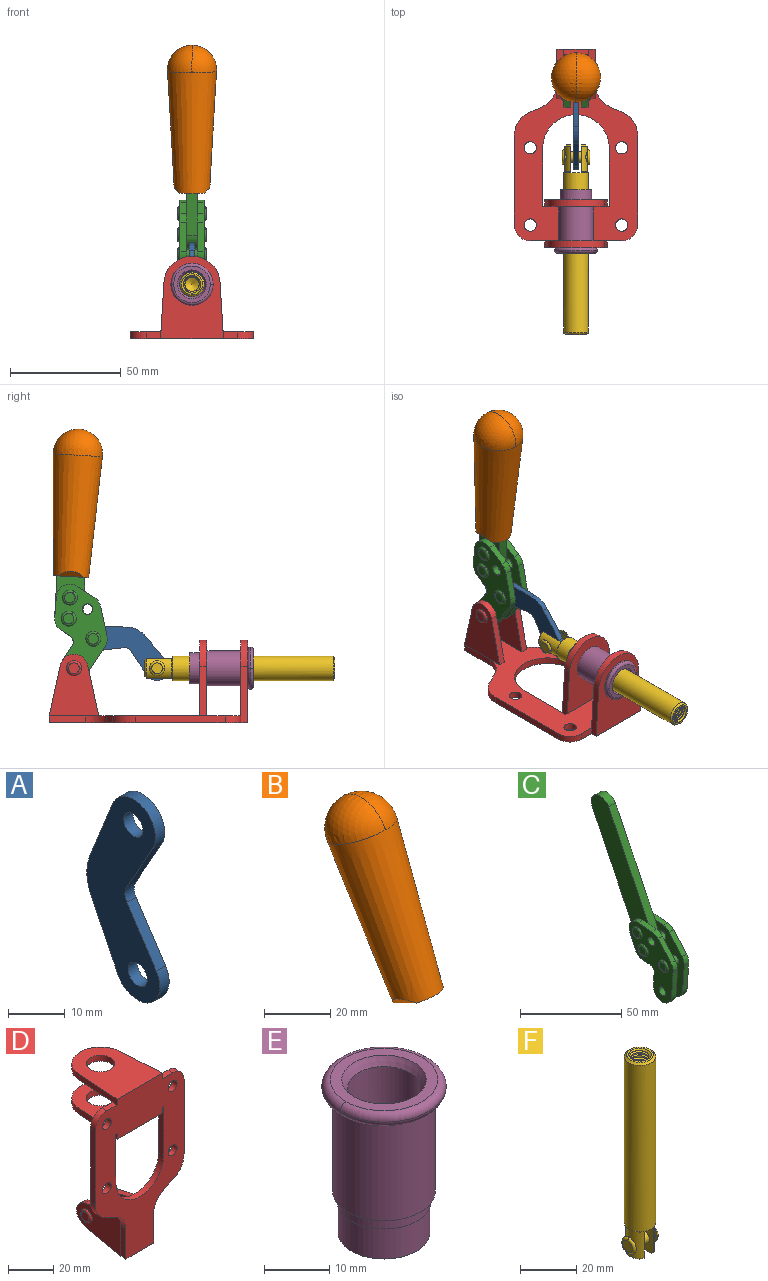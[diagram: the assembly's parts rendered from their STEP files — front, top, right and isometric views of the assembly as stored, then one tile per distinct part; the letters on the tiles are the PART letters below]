
ASSEMBLY  parts=6 mates=6
PART A: 12 faces, bbox 2.3x18.2x42.8 mm
  f0: cylinder r=2.4mm len=4.8mm, axis (1,0,0), area 34.9mm2, adj f4,f11
  f1: cylinder r=10.41mm len=8.47mm, axis (1,0,0), area 20.2mm2, adj f4,f9,f10,f11
  f2: cylinder r=3.05mm len=3.16mm, axis (1,0,0), area 7.7mm2, adj f4,f6,f7,f11
  f3: cylinder r=2.4mm len=4.8mm, axis (1,0,0), area 34.9mm2, adj f4,f11
  f4: plane 42.81x18.23mm, normal (-1,0,0), area 414.1mm2, adj f0,f1,f2,f3,f5,f6,f7,f8
  f5: cylinder r=5.54mm len=10.67mm, axis (1,0,0), area 41.8mm2, adj f4,f6,f10,f11
  f6: plane 11.66x6.53mm, normal (0,-0.87,-0.49), area 30.9mm2, adj f2,f4,f5,f11
  f7: plane 11.17x7.33mm, normal (0,-0.84,0.55), area 30.9mm2, adj f2,f4,f8,f11
  f8: cylinder r=5.54mm len=10.51mm, axis (1,0,0), area 41.8mm2, adj f4,f7,f9,f11
  f9: plane 13.67x6.67mm, normal (0,0.9,-0.44), area 35.1mm2, adj f1,f4,f8,f11
  f10: plane 14.1x5.7mm, normal (0,0.93,0.37), area 35.1mm2, adj f1,f4,f5,f11
  f11: plane 42.81x18.23mm, normal (1,0,0), area 414.1mm2, adj f0,f1,f2,f3,f5,f6,f7,f8
PART B: 11 faces, bbox 22.3x42.6x64.5 mm
  f0: sphere r=11.13mm, area 411.4mm2, adj f1,f8
  f1: cone r=11.11mm half-angle=3.3deg, axis (0,0.44,0.9), area 3251.8mm2, adj f0,f7,f8,f9,f10
  f2: cylinder r=6.16mm len=11.7mm, axis (1,0,0), area 89.5mm2, adj f3,f4,f5,f6
  f3: plane 60.23x36.75mm, normal (-1,0,0), area 763.6mm2, adj f2,f4,f6,f10
  f4: plane 51.37x25.05mm, normal (0,0.9,-0.44), area 264.2mm2, adj f2,f3,f5,f10
  f5: plane 60.23x36.75mm, normal (1,0,0), area 763.6mm2, adj f2,f4,f6,f10
  f6: plane 51.37x25.05mm, normal (0,-0.9,0.44), area 264.2mm2, adj f2,f3,f5,f10
  f7: plane 9.95x5.95mm, normal (0.71,-0.31,-0.64), area 25.8mm2, adj f1,f10
  f8: sphere r=11.13mm, area 411.4mm2, adj f0,f1
  f9: plane 9.95x5.95mm, normal (-0.71,-0.31,-0.64), area 25.8mm2, adj f1,f10
  f10: plane 14.27x11.38mm, normal (0,-0.44,-0.9), area 106.7mm2, adj f1,f3,f4,f5,f6,f7,f9
PART C: 59 faces, bbox 12.9x60.2x99.6 mm
  f0: torus R=2.39mm, axis (-1,0,0), area 14.9mm2, adj f20,f43,f51
  f1: torus R=2.39mm, axis (-1,0,0), area 14.9mm2, adj f19,f42,f51
  f2: torus R=2.39mm, axis (-1,0,0), area 14.9mm2, adj f18,f35,f51
  f3: torus R=2.39mm, axis (-1,0,0), area 14.9mm2, adj f14,f17,f23
  f4: torus R=2.39mm, axis (-1,0,0), area 14.9mm2, adj f13,f16,f23
  f5: torus R=2.39mm, axis (-1,0,0), area 14.9mm2, adj f12,f15,f23
  f6: cylinder r=2.39mm len=4.78mm, axis (1,0,0), area 46.5mm2, adj f48,f50,f51
  f7: cylinder r=2.39mm len=4.78mm, axis (1,0,0), area 46.5mm2, adj f50,f51
  f8: cylinder r=6.35mm len=12.68mm, axis (1,0,0), area 61.8mm2, adj f38,f39,f50,f51
  f9: cylinder r=2.39mm len=4.78mm, axis (-1,0,0), area 70.5mm2, adj f46,f50
  f10: cylinder r=2.39mm len=4.78mm, axis (-1,0,0), area 46.5mm2, adj f23,f45,f46
  f11: cylinder r=2.39mm len=4.78mm, axis (-1,0,0), area 46.5mm2, adj f23,f46
  f12: plane 4.78x4.78mm, normal (1,0,0), area 17.9mm2, adj f5,f15
  f13: plane 4.78x4.78mm, normal (1,0,0), area 17.9mm2, adj f4,f16
  f14: plane 4.78x4.78mm, normal (1,0,0), area 17.9mm2, adj f3,f17
  f15: torus R=2.39mm, axis (-1,0,0), area 14.9mm2, adj f5,f12,f23
  f16: torus R=2.39mm, axis (-1,0,0), area 14.9mm2, adj f4,f13,f23
  f17: torus R=2.39mm, axis (-1,0,0), area 14.9mm2, adj f3,f14,f23
  f18: plane 4.78x4.78mm, normal (-1,0,0), area 17.9mm2, adj f2,f35
  f19: plane 4.78x4.78mm, normal (-1,0,0), area 17.9mm2, adj f1,f42
  f20: plane 4.78x4.78mm, normal (-1,0,0), area 17.9mm2, adj f0,f43
  f21: plane 2.26x0.2mm, normal (1,0,0), area 0.2mm2, adj f31,f44
  f22: plane 2.26x0.2mm, normal (-1,0,0), area 0.2mm2, adj f41,f44
  f23: plane 39.37x30.77mm, normal (1,0,0), area 565.5mm2, adj f3,f4,f5,f10,f11,f15,f16,f17
  f24: cylinder r=6.1mm len=4.15mm, axis (-1,0,0), area 14.7mm2, adj f23,f25,f32,f46
  f25: plane 10.25x9.01mm, normal (0,-0.75,0.66), area 42.3mm2, adj f23,f24,f26,f46
  f26: cylinder r=6.35mm len=4.64mm, axis (-1,0,0), area 15.6mm2, adj f23,f25,f27,f46
  f27: plane 15.84x3.1mm, normal (0,-1,-0.07), area 49.2mm2, adj f23,f26,f28,f46
  f28: cylinder r=6.35mm len=12.68mm, axis (-1,0,0), area 61.8mm2, adj f23,f27,f29,f46
  f29: plane 8.11x3.1mm, normal (0,1,0.07), area 25.2mm2, adj f23,f28,f30,f46
  f30: cylinder r=3.05mm len=3.25mm, axis (-1,0,0), area 14.8mm2, adj f23,f29,f31,f46
  f31: plane 5.99x3.1mm, normal (0,0.07,-1), area 18.6mm2, adj f21,f23,f30,f44,f46
  f32: plane 9.5x3.1mm, normal (0,-0.07,1), area 29.5mm2, adj f23,f24,f33,f46,f47
  f33: cylinder r=6.1mm len=8.63mm, axis (-1,0,0), area 39.1mm2, adj f23,f32,f34,f47
  f34: plane 8.65x3.96mm, normal (0,0.91,-0.42), area 29.5mm2, adj f23,f33,f44,f47
  f35: torus R=2.39mm, axis (-1,0,0), area 14.9mm2, adj f2,f18,f51
  f36: plane 10.25x9.01mm, normal (0,-0.75,0.66), area 42.3mm2, adj f37,f49,f50,f51
  f37: cylinder r=6.35mm len=4.64mm, axis (1,0,0), area 15.6mm2, adj f36,f38,f50,f51
  f38: plane 15.84x3.1mm, normal (0,-1,-0.07), area 49.2mm2, adj f8,f37,f50,f51
  f39: plane 8.11x3.1mm, normal (0,1,0.07), area 25.2mm2, adj f8,f40,f50,f51
  f40: cylinder r=3.05mm len=3.25mm, axis (1,0,0), area 14.8mm2, adj f39,f41,f50,f51
  f41: plane 5.99x3.1mm, normal (0,0.07,-1), area 18.6mm2, adj f22,f40,f44,f50,f51
  f42: torus R=2.39mm, axis (-1,0,0), area 14.9mm2, adj f1,f19,f51
  f43: torus R=2.39mm, axis (-1,0,0), area 14.9mm2, adj f0,f20,f51
  f44: cylinder r=6.35mm len=12.12mm, axis (-1,0,0), area 128.9mm2, adj f21,f22,f23,f31,f34,f41,f46,f47
  f45: plane 2.65x1.35mm, normal (1,0,0), area 1mm2, adj f10,f55
  f46: plane 39.08x20.42mm, normal (-1,0,0), area 412.5mm2, adj f9,f10,f11,f24,f25,f26,f27,f28
  f47: plane 77.62x39.82mm, normal (1,0,0), area 850mm2, adj f32,f33,f34,f44,f53,f54,f55
  f48: plane 2.65x1.35mm, normal (-1,0,0), area 1mm2, adj f6,f55
  f49: cylinder r=6.1mm len=4.15mm, axis (1,0,0), area 14.7mm2, adj f36,f50,f51,f56
  f50: plane 39.08x20.42mm, normal (1,0,0), area 412.5mm2, adj f6,f7,f8,f9,f36,f37,f38,f39
  f51: plane 39.37x30.77mm, normal (-1,0,0), area 565.5mm2, adj f0,f1,f2,f6,f7,f8,f35,f36
  f52: plane 8.65x3.96mm, normal (0,0.91,-0.42), area 29.5mm2, adj f44,f51,f57,f58
  f53: plane 68.49x33.4mm, normal (0,0.9,-0.44), area 358.1mm2, adj f44,f47,f54,f58
  f54: cylinder r=6.35mm len=12.06mm, axis (1,0,0), area 93.7mm2, adj f47,f53,f55,f58
  f55: plane 68.49x33.4mm, normal (0,-0.9,0.44), area 358.1mm2, adj f44,f45,f46,f47,f48,f50,f54,f58
  f56: plane 9.5x3.1mm, normal (0,-0.07,1), area 29.5mm2, adj f49,f50,f51,f57,f58
  f57: cylinder r=6.1mm len=8.63mm, axis (1,0,0), area 39.1mm2, adj f51,f52,f56,f58
  f58: plane 77.62x39.82mm, normal (-1,0,0), area 850mm2, adj f44,f52,f53,f54,f55,f56,f57
PART D: 55 faces, bbox 55.7x37.4x89.8 mm
  f0: torus R=2.41mm, axis (-1,0,0), area 15mm2, adj f11,f15,f25
  f1: torus R=2.41mm, axis (-1,0,0), area 15mm2, adj f10,f12,f22
  f2: cylinder r=2.78mm len=5.56mm, axis (0,-1,0), area 54.2mm2, adj f30,f54
  f3: cylinder r=14.99mm len=29.97mm, axis (0,-1,0), area 145.9mm2, adj f30,f49,f53,f54
  f4: cylinder r=2.78mm len=5.56mm, axis (0,-1,0), area 54.2mm2, adj f30,f54
  f5: cylinder r=2.78mm len=5.56mm, axis (0,-1,0), area 54.2mm2, adj f30,f54
  f6: cylinder r=2.78mm len=5.56mm, axis (0,-1,0), area 54.2mm2, adj f30,f54
  f7: cylinder r=6.35mm len=12.7mm, axis (0,0,1), area 123.6mm2, adj f27,f51
  f8: cylinder r=6.35mm len=12.7mm, axis (0,0,-1), area 124.7mm2, adj f21,f35
  f9: cylinder r=2.41mm len=11.18mm, axis (-1,0,0), area 169.4mm2, adj f16,f19
  f10: plane 4.83x4.83mm, normal (1,0,0), area 18.3mm2, adj f1,f12
  f11: plane 4.83x4.83mm, normal (-1,0,0), area 18.3mm2, adj f0,f15
  f12: torus R=2.41mm, axis (-1,0,0), area 15mm2, adj f1,f10,f22
  f13: cylinder r=6.35mm len=12.41mm, axis (1,0,0), area 53.4mm2, adj f18,f19,f22,f23
  f14: cylinder r=6.35mm len=12.41mm, axis (-1,0,0), area 53.4mm2, adj f16,f17,f24,f25
  f15: torus R=2.41mm, axis (-1,0,0), area 15mm2, adj f0,f11,f25
  f16: plane 27.86x22.35mm, normal (1,0,0), area 425.4mm2, adj f9,f14,f17,f24,f30
  f17: plane 22.86x4.97mm, normal (0,0.21,0.98), area 72.5mm2, adj f14,f16,f25,f30
  f18: plane 22.86x4.97mm, normal (0,0.21,0.98), area 72.5mm2, adj f13,f19,f22,f30
  f19: plane 27.86x22.35mm, normal (-1,0,0), area 425.4mm2, adj f9,f13,f18,f23,f30
  f20: cylinder r=12.7mm len=25.35mm, axis (0,0,-1), area 119.8mm2, adj f21,f34,f35,f36
  f21: plane 34.21x28.07mm, normal (0,0,-1), area 702.4mm2, adj f8,f20,f30,f34,f36
  f22: plane 27.96x22.45mm, normal (1,0,0), area 407.2mm2, adj f1,f12,f13,f18,f23,f30,f42,f43
  f23: plane 22.86x4.97mm, normal (0,0.21,-0.98), area 72.5mm2, adj f13,f19,f22,f44
  f24: plane 22.86x4.97mm, normal (0,0.21,-0.98), area 72.5mm2, adj f14,f16,f25,f44
  f25: plane 27.86x22.35mm, normal (-1,0,0), area 407.1mm2, adj f0,f14,f15,f17,f24,f30,f45,f46
  f26: plane 3.1x0.95mm, normal (0,0,-1), area 2.7mm2, adj f30,f49,f50,f54
  f27: plane 34.21x28.07mm, normal (0,0,1), area 702.4mm2, adj f7,f28,f30,f50,f52
  f28: cylinder r=12.7mm len=25.35mm, axis (0,0,1), area 118.8mm2, adj f27,f50,f51,f52
  f29: plane 3.1x0.95mm, normal (0,0,-1), area 2.7mm2, adj f30,f52,f53,f54
  f30: plane 86.54x55.63mm, normal (0,1,0), area 2362.9mm2, adj f2,f3,f4,f5,f6,f16,f17,f18
  f31: plane 40.56x3.1mm, normal (-1,0,0), area 125.7mm2, adj f30,f32,f48,f54
  f32: cylinder r=7.11mm len=7.11mm, axis (0,-1,0), area 34.6mm2, adj f30,f31,f33,f54
  f33: plane 6.67x3.1mm, normal (0,0,1), area 20.4mm2, adj f30,f32,f34,f54
  f34: plane 25.39x3.13mm, normal (-1,0.06,0), area 79.5mm2, adj f20,f21,f33,f35,f54
  f35: plane 37.31x28.45mm, normal (0,0,1), area 789.9mm2, adj f8,f20,f34,f36,f54
  f36: plane 25.39x3.13mm, normal (1,0.06,0), area 79.5mm2, adj f20,f21,f35,f37,f54
  f37: plane 6.67x3.1mm, normal (0,0,1), area 20.4mm2, adj f30,f36,f38,f54
  f38: cylinder r=7.11mm len=7.11mm, axis (0,-1,0), area 34.6mm2, adj f30,f37,f39,f54
  f39: plane 40.56x3.1mm, normal (1,0,0), area 125.7mm2, adj f30,f38,f40,f54
  f40: cylinder r=11.18mm len=10.16mm, axis (0,-1,0), area 39.5mm2, adj f30,f39,f41,f54
  f41: plane 6.09x3.1mm, normal (0.42,0,-0.91), area 20.8mm2, adj f30,f40,f42,f54
  f42: cylinder r=11.18mm len=9.41mm, axis (0,-1,0), area 37.2mm2, adj f22,f30,f41,f43,f54
  f43: plane 16.5x3.1mm, normal (1,0,0), area 51.1mm2, adj f22,f42,f44,f54
  f44: plane 17.37x3.1mm, normal (0,0,-1), area 53.8mm2, adj f23,f24,f30,f43,f45,f54
  f45: plane 16.5x3.1mm, normal (-1,0,0), area 51.1mm2, adj f25,f44,f46,f54
  f46: cylinder r=11.18mm len=9.41mm, axis (0,-1,0), area 37.2mm2, adj f25,f30,f45,f47,f54
  f47: plane 6.09x3.1mm, normal (-0.42,0,-0.91), area 20.8mm2, adj f30,f46,f48,f54
  f48: cylinder r=11.18mm len=10.16mm, axis (0,-1,0), area 39.5mm2, adj f30,f31,f47,f54
  f49: plane 26.54x3.1mm, normal (-1,0,0), area 82.3mm2, adj f3,f26,f30,f54
  f50: plane 25.39x3.1mm, normal (1,0.06,0), area 78.8mm2, adj f26,f27,f28,f51,f54
  f51: plane 37.31x28.45mm, normal (0,0,-1), area 789.9mm2, adj f7,f28,f50,f52,f54
  f52: plane 25.39x3.1mm, normal (-1,0.06,0), area 78.8mm2, adj f27,f28,f29,f51,f54
  f53: plane 26.54x3.1mm, normal (1,0,0), area 82.3mm2, adj f3,f29,f30,f54
  f54: plane 89.66x55.63mm, normal (0,-1,0), area 2678.5mm2, adj f2,f3,f4,f5,f6,f26,f29,f31
PART E: 15 faces, bbox 20.6x20.6x28.7 mm
  f0: torus R=8.26mm, axis (0,0,1), area 56.8mm2, adj f1,f10,f12
  f1: torus R=8.26mm, axis (0,0,1), area 56.8mm2, adj f0,f6,f13
  f2: cylinder r=5.59mm len=25.91mm, axis (0,0,1), area 909.6mm2, adj f3,f4
  f3: cone r=6.86mm half-angle=45deg, axis (0,0,-1), area 70.2mm2, adj f2,f14
  f4: cone r=6.47mm half-angle=30deg, axis (0,0,1), area 66.7mm2, adj f2,f13
  f5: cylinder r=7.04mm len=14.07mm, axis (0,0,1), area 252.6mm2, adj f11,f14
  f6: torus R=8.26mm, axis (0,0,1), area 56.8mm2, adj f1,f12,f13
  f7: cylinder r=7.16mm len=14.33mm, axis (0,0,1), area 91.5mm2, adj f9,f11
  f8: cylinder r=7.86mm len=18.42mm, axis (0,0,1), area 909.6mm2, adj f9,f10
  f9: plane 15.72x15.72mm, normal (0,0,-1), area 33mm2, adj f7,f8
  f10: plane 16.51x16.51mm, normal (0,0,-1), area 19.9mm2, adj f0,f8,f12
  f11: plane 14.33x14.33mm, normal (0,0,-1), area 5.7mm2, adj f5,f7
  f12: torus R=8.26mm, axis (0,0,1), area 56.8mm2, adj f0,f6,f10
  f13: plane 16.51x16.51mm, normal (0,0,1), area 82.7mm2, adj f1,f4,f6
  f14: plane 14.07x14.07mm, normal (0,0,-1), area 7.8mm2, adj f3,f5
PART F: 48 faces, bbox 12.6x11.1x86.1 mm
  f0: torus R=2.41mm, axis (-1,0,0), area 15mm2, adj f30,f32,f34
  f1: torus R=2.41mm, axis (-1,0,0), area 15mm2, adj f29,f31,f33
  f2: cylinder r=5.54mm len=72.39mm, axis (0,0,1), area 2518.5mm2, adj f3,f4,f42,f43
  f3: cone r=5.54mm half-angle=45deg, axis (0,0,1), area 7.6mm2, adj f2,f5,f41
  f4: cone r=5.54mm half-angle=45deg, axis (0,0,-1), area 34.9mm2, adj f2,f39
  f5: cylinder r=5.08mm len=11.48mm, axis (0,0,1), area 108.3mm2, adj f3,f7,f8,f41
  f6: cylinder r=2.41mm len=4.83mm, axis (-1,0,0), area 71.2mm2, adj f40,f41
  f7: cylinder r=2.41mm len=4.83mm, axis (-1,0,0), area 7.6mm2, adj f5,f34
  f8: cone r=5.08mm half-angle=45deg, axis (0,0,1), area 10.6mm2, adj f5,f37,f41
  f9: cone r=3.98mm half-angle=45deg, axis (0,0,1), area 17.6mm2, adj f27,f39,f45,f46,f47
  f10: cylinder r=2.41mm len=4.83mm, axis (-1,0,0), area 7.6mm2, adj f33,f38
  f11: cylinder r=3.2mm len=6.4mm, axis (0,0,1), area 78.4mm2, adj f12,f28,f44,f45,f47
  f12: cylinder r=3.2mm len=6.4mm, axis (0,0,1), area 10.5mm2, adj f11,f13,f45,f47
  f13: cylinder r=3.2mm len=6.4mm, axis (0,0,1), area 10.5mm2, adj f12,f14,f45,f47
  f14: cylinder r=3.2mm len=6.4mm, axis (0,0,1), area 10.5mm2, adj f13,f15,f45,f47
  f15: cylinder r=3.2mm len=6.4mm, axis (0,0,1), area 10.5mm2, adj f14,f16,f45,f47
  f16: cylinder r=3.2mm len=6.4mm, axis (0,0,1), area 10.5mm2, adj f15,f17,f45,f47
  f17: cylinder r=3.2mm len=6.4mm, axis (0,0,1), area 10.5mm2, adj f16,f18,f45,f47
  f18: cylinder r=3.2mm len=6.4mm, axis (0,0,1), area 10.5mm2, adj f17,f19,f45,f47
  f19: cylinder r=3.2mm len=6.4mm, axis (0,0,1), area 10.5mm2, adj f18,f20,f45,f47
  f20: cylinder r=3.2mm len=6.4mm, axis (0,0,1), area 10.5mm2, adj f19,f21,f45,f47
  f21: cylinder r=3.2mm len=6.4mm, axis (0,0,1), area 10.5mm2, adj f20,f22,f45,f47
  f22: cylinder r=3.2mm len=6.4mm, axis (0,0,1), area 10.5mm2, adj f21,f23,f45,f47
  f23: cylinder r=3.2mm len=6.4mm, axis (0,0,1), area 10.5mm2, adj f22,f24,f45,f47
  f24: cylinder r=3.2mm len=6.4mm, axis (0,0,1), area 10.5mm2, adj f23,f25,f45,f47
  f25: cylinder r=3.2mm len=6.4mm, axis (0,0,1), area 10.5mm2, adj f24,f26,f45,f47
  f26: cylinder r=3.2mm len=6.4mm, axis (0,0,1), area 10.5mm2, adj f25,f27,f45,f47
  f27: cylinder r=3.2mm len=6.4mm, axis (0,0,1), area 7.4mm2, adj f9,f26,f45,f47
  f28: cone r=3.2mm half-angle=60deg, axis (0,0,1), area 37.2mm2, adj f11
  f29: plane 4.83x4.83mm, normal (-1,0,0), area 18.3mm2, adj f1,f31
  f30: plane 4.83x4.83mm, normal (1,0,0), area 18.3mm2, adj f0,f32
  f31: torus R=2.41mm, axis (-1,0,0), area 15mm2, adj f1,f29,f33
  f32: torus R=2.41mm, axis (-1,0,0), area 15mm2, adj f0,f30,f34
  f33: plane 6.83x6.83mm, normal (1,0,0), area 18.3mm2, adj f1,f10,f31
  f34: plane 6.83x6.83mm, normal (-1,0,0), area 18.3mm2, adj f0,f7,f32
  f35: cone r=5.08mm half-angle=45deg, axis (0,0,1), area 10.6mm2, adj f36,f38,f40
  f36: plane 7.25x1.97mm, normal (0,0,-1), area 10mm2, adj f35,f40
  f37: plane 7.25x1.97mm, normal (0,0,-1), area 10mm2, adj f8,f41
  f38: cylinder r=5.08mm len=11.48mm, axis (0,0,1), area 108.3mm2, adj f10,f35,f40,f42
  f39: plane 9.55x9.55mm, normal (0,0,1), area 22mm2, adj f4,f9
  f40: plane 12.76x10.09mm, normal (1,0,0), area 95.7mm2, adj f6,f35,f36,f38,f42,f43
  f41: plane 12.76x10.09mm, normal (-1,0,0), area 95.7mm2, adj f3,f5,f6,f8,f37,f43
  f42: cone r=5.54mm half-angle=45deg, axis (0,0,1), area 7.6mm2, adj f2,f38,f40
  f43: plane 11.07x4.7mm, normal (0,0,-1), area 50.4mm2, adj f2,f40,f41
  f44: plane 0.89x0.62mm, normal (-1,0,0), area 0.3mm2, adj f11,f45,f46,f47
  f45: bspline ~24.8x7.63mm, area 266.6mm2, adj f9,f11,f12,f13,f14,f15,f16,f17
  f46: bspline ~24.87x7.63mm, area 73.6mm2, adj f9,f44,f45,f47
  f47: bspline ~24.98x7.63mm, area 272.5mm2, adj f9,f11,f12,f13,f14,f15,f16,f17
PLACE A rot(axis=(1,0,0),116.7deg) t=(0,28.59,9.59)mm
PLACE B rot(axis=(1,0,0),29.2deg) t=(0,4.09,40.61)mm
PLACE C rot(axis=(1,0,0),29.2deg) t=(0,4.09,40.61)mm
PLACE D rot(axis=(1,0,0),90deg) t=(0,9.14,0)mm fixed
PLACE E rot(axis=(1,0,0),90deg) t=(0,9.14,0)mm
PLACE F rot(axis=(1,0,0),90deg) t=(0,19.17,0)mm
MATE revolute A.f5 <-> F.f6  axis (1,0,0) through (0,3.7,24.61)mm
MATE fastened C.f54 <-> B.f2  axis (1,0,0) through (0,39.36,123.09)mm
MATE revolute C.f4 <-> A.f3  axis (-1,0,0) through (0,32.54,37.89)mm
MATE revolute D.f0 <-> C.f7  axis (-1,0,0) through (0,41.23,24.61)mm
MATE slider F.f2 <-> D.f7  axis (0,-1,0) through (0,-39.61,24.61)mm
MATE fastened D.f7 <-> E.f0  axis (0,-1,0) through (0,-37.25,24.61)mm
